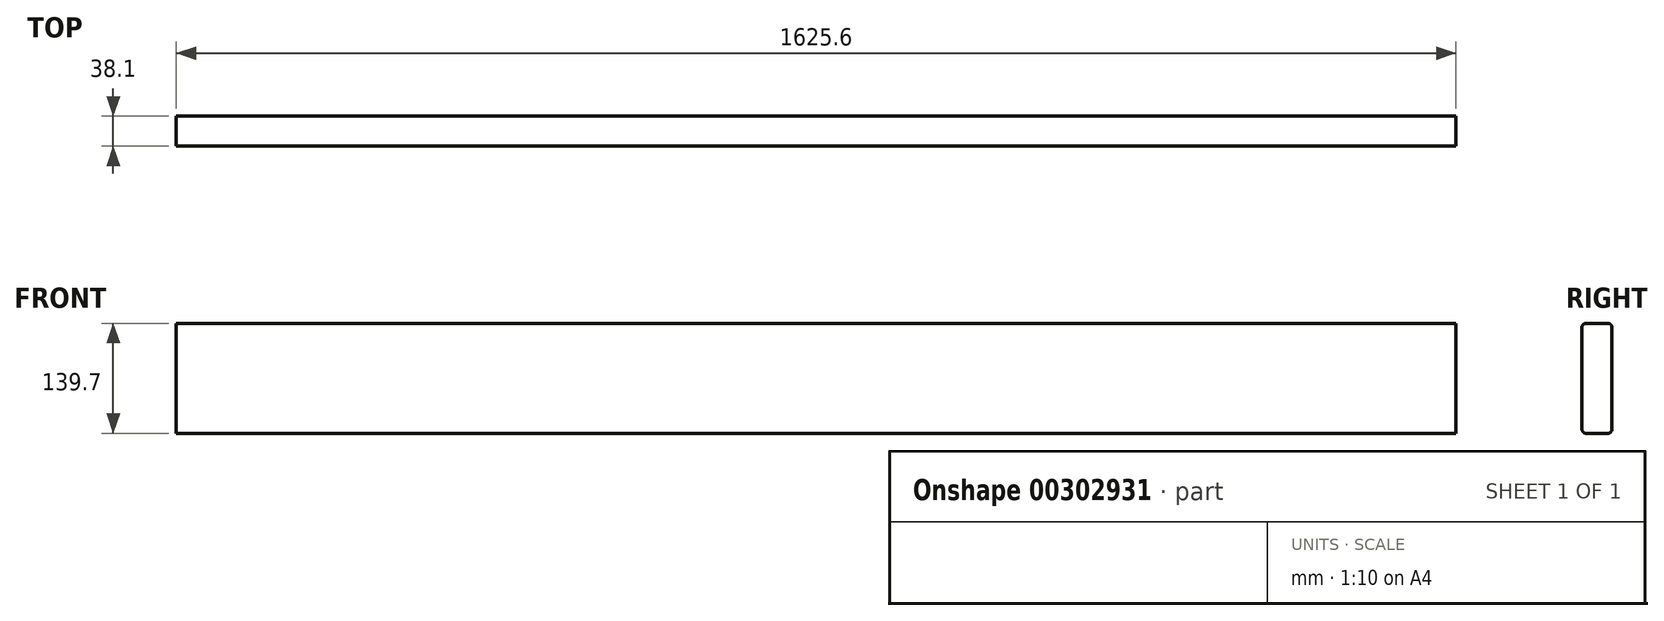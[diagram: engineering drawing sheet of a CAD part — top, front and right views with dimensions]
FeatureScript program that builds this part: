
annotation { "Feature Type Name" : "Feature", "Feature Type Description" : "" }
export const myFeature = defineFeature(function(context is Context, id is Id, definition is map)
    precondition{}
    {
        {
            var Q0;
            Q0=qCreatedBy(makeId("Front.planeOp"),FACE);
            var sketch = newSketch(context, id + "F0", { "sketchPlane" : qUnion([Q0])});
            skLineSegment(sketch, "E0.bottom", {"start": v(812.8, -69.85) * mm, "end": v(-812.8, -69.85) * mm});
            skLineSegment(sketch, "E0.top", {"start": v(812.8, 69.85) * mm, "end": v(-812.8, 69.85) * mm});
            skLineSegment(sketch, "E0.left", {"start": v(812.8, -69.85) * mm, "end": v(812.8, 69.85) * mm});
            skLineSegment(sketch, "E0.right", {"start": v(-812.8, -69.85) * mm, "end": v(-812.8, 69.85) * mm});
            skPoint(sketch, "E0.middle", {"position": v(0, 0) * mm});
            skSolve(sketch);
        }
        {
            var Q0;
            Q0 = qSketchRegion(id + "F0", true);
            extrude(context, id + "F1", {"entities" : qUnion([Q0]), "endBound" : BoundingType.SYMMETRIC, "depth" : 38.1 * mm});
        }
        {
            var Q0;
            Q0=makeQuery(id+"F1.opExtrude","CAP_EDGE",EDGE,{"disambiguationData":[OSD([sQuery(id+"F0.wireOp",EDGE,"E0.top")])],"isStart":false});
            var Q1;
            Q1=makeQuery(id+"F1.opExtrude","CAP_EDGE",EDGE,{"disambiguationData":[OSD([sQuery(id+"F0.wireOp",EDGE,"E0.top")])],"isStart":true});
            var Q2;
            Q2=makeQuery(id+"F1.opExtrude","CAP_EDGE",EDGE,{"disambiguationData":[OSD([sQuery(id+"F0.wireOp",EDGE,"E0.bottom")])],"isStart":true});
            var Q3;
            Q3=makeQuery(id+"F1.opExtrude","CAP_EDGE",EDGE,{"disambiguationData":[OSD([sQuery(id+"F0.wireOp",EDGE,"E0.bottom")])],"isStart":false});
            fillet(context, id + "F2", {"entities" : qUnion([Q0, Q1, Q2, Q3]), "radius" : 5.08 * mm, "tangentPropagation" : true, "allowEdgeOverflow" : false});
        }
    });
